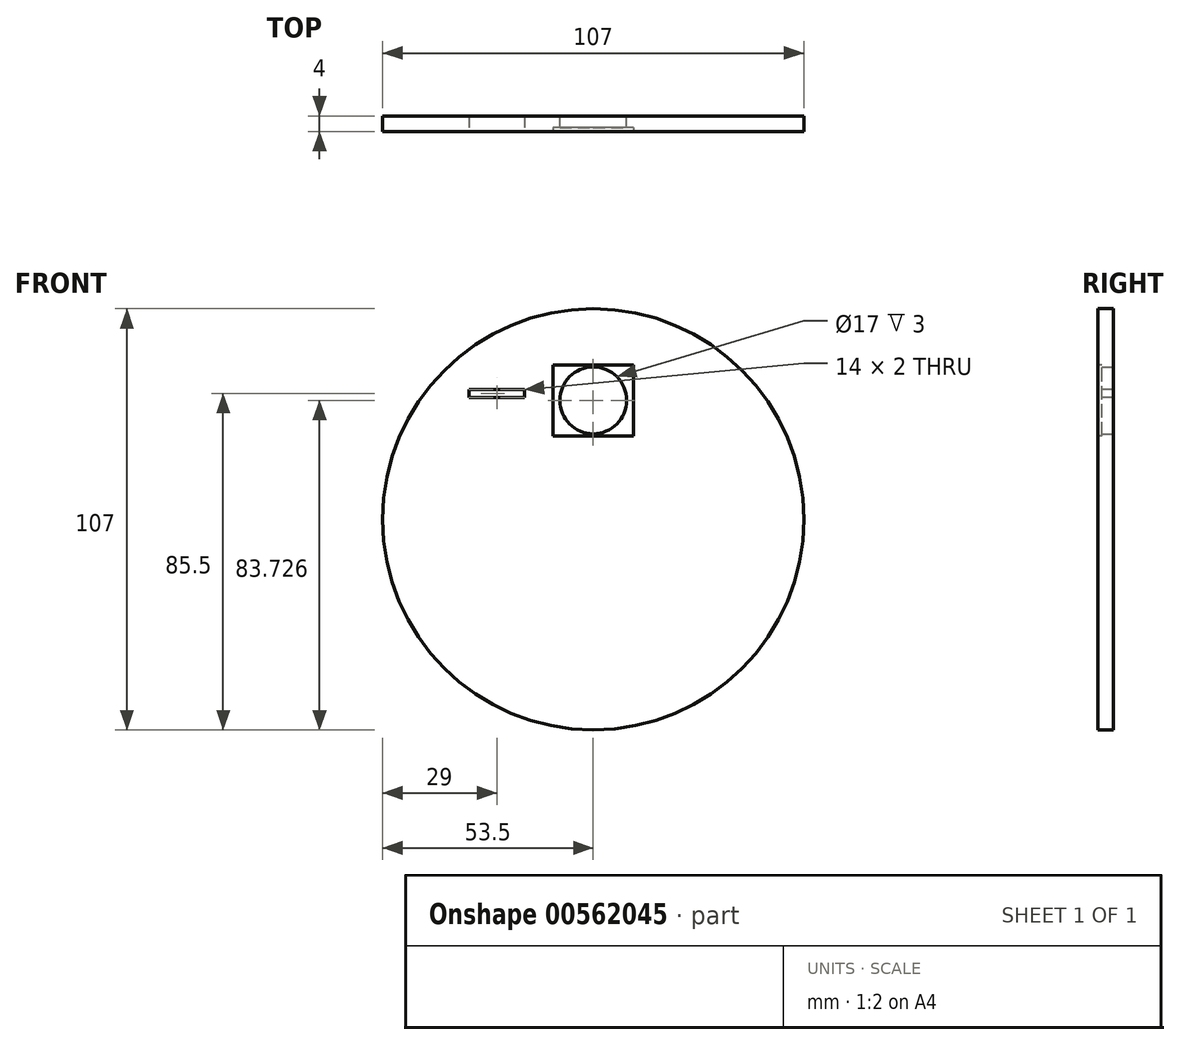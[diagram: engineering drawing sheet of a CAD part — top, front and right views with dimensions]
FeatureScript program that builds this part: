
annotation { "Feature Type Name" : "Feature", "Feature Type Description" : "" }
export const myFeature = defineFeature(function(context is Context, id is Id, definition is map)
    precondition{}
    {
        {
            var Q0;
            Q0=qCreatedBy(makeId("Front.planeOp"),FACE);
            var sketch = newSketch(context, id + "F0", { "sketchPlane" : qUnion([Q0])});
            skCircle(sketch, "E0", {"center": v(0, 0) * mm, "radius": 53.5 * mm});
            skCircle(sketch, "E1", {"center": v(0, 30.23) * mm, "radius": 8.5 * mm});
            skSolve(sketch);
        }
        {
            var Q0;
            Q0=makeQuery(id+"F0.imprint","IMPRINT",FACE,{"disambiguationData":[TD([[makeQuery(id+"F0.imprint","IMPRINT",EDGE,{"derivedFrom":sQuery(id+"F0.wireOp",EDGE,"E0")}),1.0]])]});
            extrude(context, id + "F1", {"entities" : qUnion([Q0]), "depth" : 4 * mm, "offsetDistance" : 25 * mm});
        }
        {
            var Q0;
            Q0=makeQuery(id+"F1.opExtrude","CAP_FACE",FACE,{"disambiguationData":[OSD([sQuery(id+"F0.wireOp",EDGE,"E0"),sQuery(id+"F0.wireOp",EDGE,"saq27g7c-3m0G-zHqF-X7Gi-2weGeJ5qwx4z")])],"isStart":false});
            var sketch = newSketch(context, id + "F2", { "sketchPlane" : qUnion([Q0])});
            skLineSegment(sketch, "E2.bottom", {"start": v(10.25, 21.23) * mm, "end": v(-10.25, 21.23) * mm});
            skLineSegment(sketch, "E2.top", {"start": v(10.25, 39.23) * mm, "end": v(-10.25, 39.23) * mm});
            skLineSegment(sketch, "E2.left", {"start": v(10.25, 21.23) * mm, "end": v(10.25, 39.23) * mm});
            skLineSegment(sketch, "E2.right", {"start": v(-10.25, 21.23) * mm, "end": v(-10.25, 39.23) * mm});
            skPoint(sketch, "E2.middle", {"position": v(0, 30.23) * mm});
            skSolve(sketch);
        }
        {
            var Q0;
            Q0=makeQuery(id+"F2.imprint","IMPRINT",FACE,{"disambiguationData":[TD([[makeQuery(id+"F2.imprint","IMPRINT",EDGE,{"derivedFrom":sQuery(id+"F2.wireOp",EDGE,"lPkMj89T-4iQL-x7RK-NxJW-oGMJNIQ8vdm9")}),1.0]])]});
            var Q1;
            Q1=makeQuery(id+"F2.imprint","IMPRINT",FACE,{"disambiguationData":[TD([[makeQuery(id+"F2.imprint","IMPRINT",EDGE,{"derivedFrom":sQuery(id+"F2.wireOp",EDGE,"YQnCsI7F-9rE4-FCKY-HQnM-YKJW6YsEvAr6.bottom")}),-1.0]])]});
            var Q2;
            Q2=makeQuery(id+"F2.imprint","IMPRINT",FACE,{"disambiguationData":[TD([[makeQuery(id+"F2.imprint","IMPRINT",EDGE,{"derivedFrom":sQuery(id+"F2.wireOp",EDGE,"E2.bottom")}),-1.0]])]});
            extrude(context, id + "F3", {"entities" : qUnion([Q0, Q1, Q2]), "operationType" : NewBodyOperationType.REMOVE, "oppositeDirection" : true, "depth" : 1 * mm, "offsetDistance" : 25 * mm});
        }
        {
            var Q0;
            Q0=makeQuery(id+"F1.opExtrude","CAP_FACE",FACE,{"disambiguationData":[OSD([sQuery(id+"F0.wireOp",EDGE,"E0"),sQuery(id+"F0.wireOp",EDGE,"E1")])],"isStart":false});
            var sketch = newSketch(context, id + "F4", { "sketchPlane" : qUnion([Q0])});
            skLineSegment(sketch, "E3.bottom", {"start": v(-17.5, 31) * mm, "end": v(-31.5, 31) * mm});
            skLineSegment(sketch, "E3.top", {"start": v(-17.5, 33) * mm, "end": v(-31.5, 33) * mm});
            skLineSegment(sketch, "E3.left", {"start": v(-17.5, 31) * mm, "end": v(-17.5, 33) * mm});
            skLineSegment(sketch, "E3.right", {"start": v(-31.5, 31) * mm, "end": v(-31.5, 33) * mm});
            skPoint(sketch, "E3.middle", {"position": v(-24.5, 32) * mm});
            skSolve(sketch);
        }
        {
            var Q0;
            Q0=makeQuery(id+"F4.imprint","IMPRINT",FACE,{"disambiguationData":[TD([[makeQuery(id+"F4.imprint","IMPRINT",EDGE,{"derivedFrom":sQuery(id+"F4.wireOp",EDGE,"E3.bottom")}),-1.0]])]});
            var Q1;
            Q1=sQuery(id+"F4.wireOp",EDGE,"E3.left");
            var Q2;
            Q2=sQuery(id+"F4.wireOp",EDGE,"E3.right");
            var Q3;
            Q3=sQuery(id+"F4.wireOp",EDGE,"E3.bottom");
            var Q4;
            Q4=sQuery(id+"F4.wireOp",EDGE,"E3.top");
            extrude(context, id + "F5", {"entities" : qUnion([Q0]), "operationType" : NewBodyOperationType.REMOVE, "surfaceEntities" : qUnion([Q1, Q2, Q3, Q4]), "oppositeDirection" : true, "depth" : 25 * mm, "offsetDistance" : 25 * mm});
        }
    });
